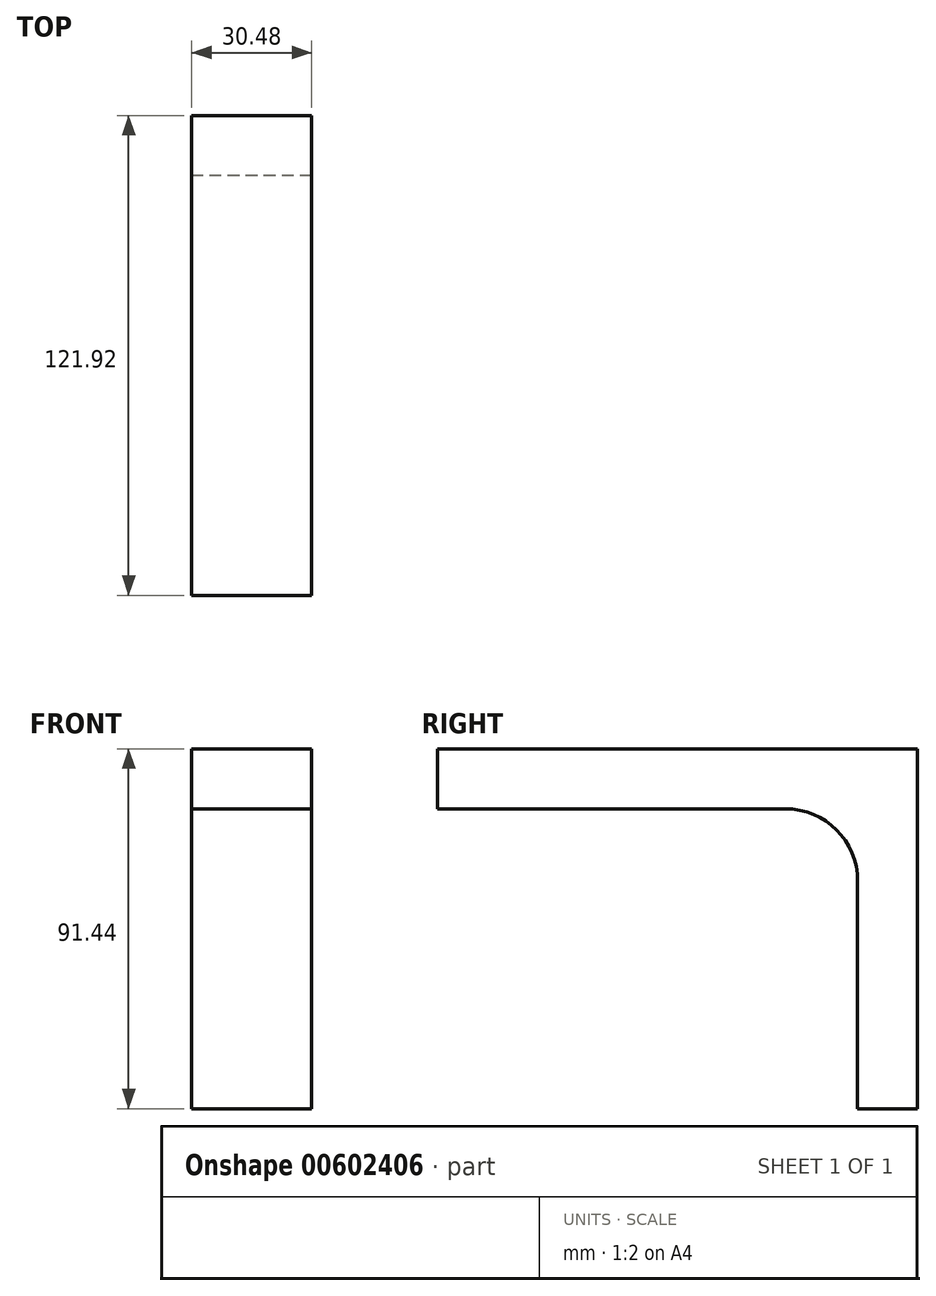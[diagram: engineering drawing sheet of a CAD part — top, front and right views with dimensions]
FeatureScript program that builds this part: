
annotation { "Feature Type Name" : "Feature", "Feature Type Description" : "" }
export const myFeature = defineFeature(function(context is Context, id is Id, definition is map)
    precondition{}
    {
        {
            var Q0;
            Q0=qCreatedBy(makeId("Right.planeOp"),FACE);
            var sketch = newSketch(context, id + "F0", { "sketchPlane" : qUnion([Q0])});
            skLineSegment(sketch, "E0", {"start": v(0, 0) * mm, "end": v(121.92, 0) * mm});
            skLineSegment(sketch, "E1", {"start": v(121.92, 0) * mm, "end": v(121.92, -91.44) * mm});
            skLineSegment(sketch, "E2", {"start": v(121.92, -91.44) * mm, "end": v(106.68, -91.44) * mm});
            skLineSegment(sketch, "E3", {"start": v(106.68, -91.44) * mm, "end": v(106.68, -15.24) * mm});
            skLineSegment(sketch, "E4", {"start": v(106.68, -15.24) * mm, "end": v(0, -15.24) * mm});
            skLineSegment(sketch, "E5", {"start": v(0, -15.24) * mm, "end": v(0, 0) * mm});
            skSolve(sketch);
        }
        {
            var Q0;
            Q0=makeQuery(id+"F0.imprint","IMPRINT",FACE,{"disambiguationData":[TD([[makeQuery(id+"F0.imprint","IMPRINT",EDGE,{"derivedFrom":sQuery(id+"F0.wireOp",EDGE,"E0")}),-1.0]])]});
            extrude(context, id + "F1", {"entities" : qUnion([Q0]), "depth" : 30.48 * mm, "offsetDistance" : 30.48 * mm});
        }
        {
            var Q0;
            Q0=makeQuery(id+"F1.opExtrude","SWEPT_EDGE",EDGE,{"disambiguationData":[OSD([sQuery(id+"F0.wireOp",EDGE,"E3"),sQuery(id+"F0.wireOp",EDGE,"E4")])]});
            fillet(context, id + "F2", {"entities" : qUnion([Q0]), "radius" : 18.4 * mm, "tangentPropagation" : true, "allowEdgeOverflow" : false});
        }
    });
